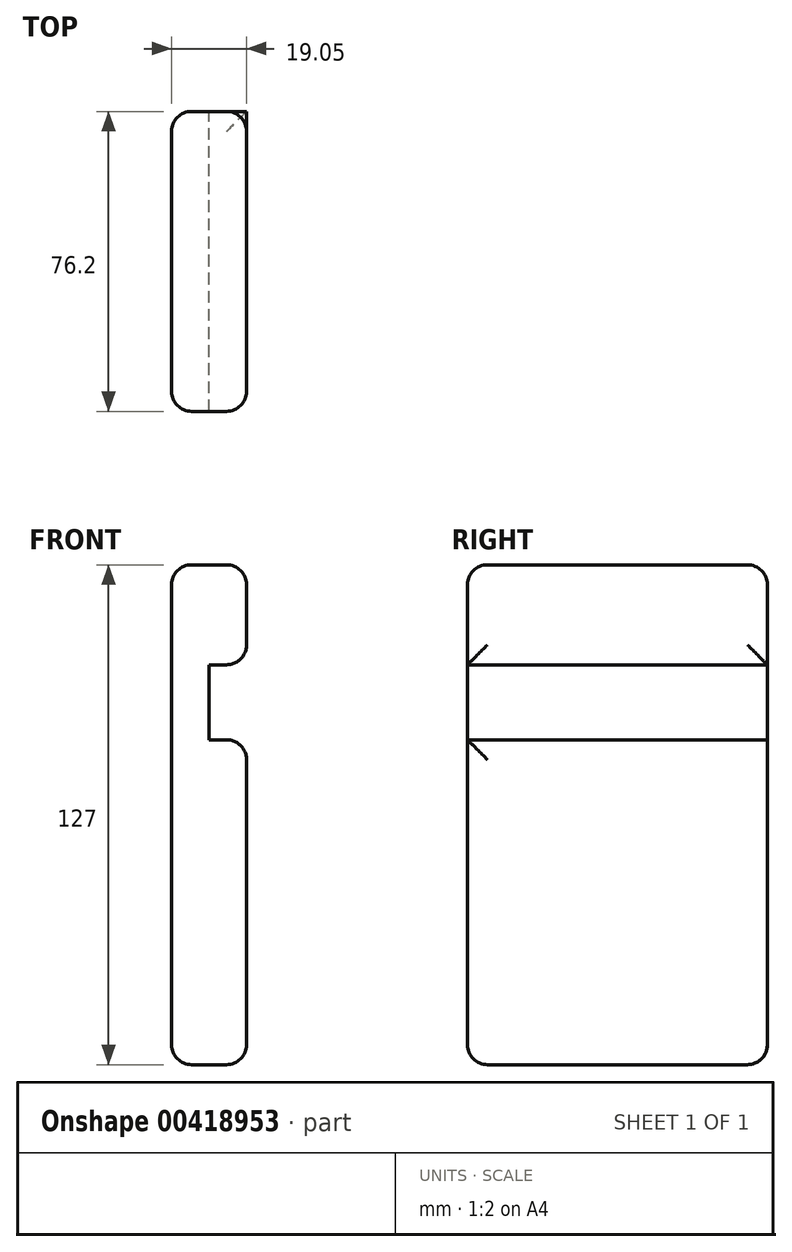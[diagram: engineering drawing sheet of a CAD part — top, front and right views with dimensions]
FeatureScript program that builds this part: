
annotation { "Feature Type Name" : "Feature", "Feature Type Description" : "" }
export const myFeature = defineFeature(function(context is Context, id is Id, definition is map)
    precondition{}
    {
        {
            var Q0;
            Q0=qCreatedBy(makeId("Front.planeOp"),FACE);
            var sketch = newSketch(context, id + "F0", { "sketchPlane" : qUnion([Q0])});
            skLineSegment(sketch, "E0.MirrorCS", {"start": v(-46.13, -71.68) * mm, "end": v(-65.18, -71.68) * mm});
            skLineSegment(sketch, "E1.MirrorCS", {"start": v(-46.13, 10.87) * mm, "end": v(-46.13, -71.68) * mm});
            skLineSegment(sketch, "E2.MirrorCS", {"start": v(-55.66, 10.87) * mm, "end": v(-46.13, 10.87) * mm});
            skLineSegment(sketch, "E3.MirrorCS", {"start": v(-55.66, 29.92) * mm, "end": v(-55.66, 10.87) * mm});
            skLineSegment(sketch, "E4.MirrorCS", {"start": v(-46.13, 29.92) * mm, "end": v(-55.66, 29.92) * mm});
            skLineSegment(sketch, "E5.MirrorCS", {"start": v(-46.13, 55.32) * mm, "end": v(-46.13, 29.92) * mm});
            skLineSegment(sketch, "E6.MirrorCS", {"start": v(-65.18, 55.32) * mm, "end": v(-46.13, 55.32) * mm});
            skLineSegment(sketch, "E7.MirrorCS", {"start": v(-65.18, -71.68) * mm, "end": v(-65.18, 55.32) * mm});
            skSolve(sketch);
        }
        {
            var Q0;
            Q0 = qSketchRegion(id + "F0", true);
            extrude(context, id + "F1", {"entities" : qUnion([Q0]), "depth" : 76.2 * mm});
        }
        {
            var Q0;
            Q0=makeQuery(id+"F1.opExtrude","CAP_EDGE",EDGE,{"disambiguationData":[OSD([sQuery(id+"F0.wireOp",EDGE,"E6.MirrorCS")])],"isStart":false});
            var Q1;
            Q1=makeQuery(id+"F1.opExtrude","CAP_EDGE",EDGE,{"disambiguationData":[OSD([sQuery(id+"F0.wireOp",EDGE,"E6.MirrorCS")])],"isStart":true});
            var Q2;
            Q2=makeQuery(id+"F1.opExtrude","CAP_EDGE",EDGE,{"disambiguationData":[OSD([sQuery(id+"F0.wireOp",EDGE,"E0.MirrorCS")])],"isStart":false});
            var Q3;
            Q3=makeQuery(id+"F1.opExtrude","SWEPT_EDGE",EDGE,{"disambiguationData":[OSD([sQuery(id+"F0.wireOp",EDGE,"E1.MirrorCS"),sQuery(id+"F0.wireOp",EDGE,"E0.MirrorCS")])]});
            var Q4;
            Q4=makeQuery(id+"F1.opExtrude","CAP_EDGE",EDGE,{"disambiguationData":[OSD([sQuery(id+"F0.wireOp",EDGE,"E0.MirrorCS")])],"isStart":true});
            var Q5;
            Q5=makeQuery(id+"F1.opExtrude","SWEPT_EDGE",EDGE,{"disambiguationData":[OSD([sQuery(id+"F0.wireOp",EDGE,"E0.MirrorCS"),sQuery(id+"F0.wireOp",EDGE,"E7.MirrorCS")])]});
            var Q6;
            Q6=makeQuery(id+"F1.opExtrude","CAP_EDGE",EDGE,{"disambiguationData":[OSD([sQuery(id+"F0.wireOp",EDGE,"E1.MirrorCS")])],"isStart":false});
            var Q7;
            Q7=makeQuery(id+"F1.opExtrude","CAP_EDGE",EDGE,{"disambiguationData":[OSD([sQuery(id+"F0.wireOp",EDGE,"E7.MirrorCS")])],"isStart":false});
            var Q8;
            Q8=makeQuery(id+"F1.opExtrude","CAP_EDGE",EDGE,{"disambiguationData":[OSD([sQuery(id+"F0.wireOp",EDGE,"E5.MirrorCS")])],"isStart":false});
            var Q9;
            Q9=makeQuery(id+"F1.opExtrude","SWEPT_EDGE",EDGE,{"disambiguationData":[OSD([sQuery(id+"F0.wireOp",EDGE,"E5.MirrorCS"),sQuery(id+"F0.wireOp",EDGE,"E4.MirrorCS")])]});
            var Q10;
            Q10=makeQuery(id+"F1.opExtrude","SWEPT_EDGE",EDGE,{"disambiguationData":[OSD([sQuery(id+"F0.wireOp",EDGE,"E1.MirrorCS"),sQuery(id+"F0.wireOp",EDGE,"E2.MirrorCS")])]});
            var Q11;
            Q11=makeQuery(id+"F1.opExtrude","SWEPT_EDGE",EDGE,{"disambiguationData":[OSD([sQuery(id+"F0.wireOp",EDGE,"E5.MirrorCS"),sQuery(id+"F0.wireOp",EDGE,"E6.MirrorCS")])]});
            var Q12;
            Q12=makeQuery(id+"F1.opExtrude","CAP_EDGE",EDGE,{"disambiguationData":[OSD([sQuery(id+"F0.wireOp",EDGE,"E5.MirrorCS")])],"isStart":true});
            var Q13;
            Q13=makeQuery(id+"F1.opExtrude","CAP_EDGE",EDGE,{"disambiguationData":[OSD([sQuery(id+"F0.wireOp",EDGE,"E7.MirrorCS")])],"isStart":true});
            var Q14;
            Q14=makeQuery(id+"F1.opExtrude","SWEPT_EDGE",EDGE,{"disambiguationData":[OSD([sQuery(id+"F0.wireOp",EDGE,"E6.MirrorCS"),sQuery(id+"F0.wireOp",EDGE,"E7.MirrorCS")])]});
            fillet(context, id + "F2", {"entities" : qUnion([Q0, Q1, Q2, Q3, Q4, Q5, Q6, Q7, Q8, Q9, Q10, Q11, Q12, Q13, Q14]), "radius" : 5.08 * mm, "tangentPropagation" : true, "allowEdgeOverflow" : false});
        }
    });
